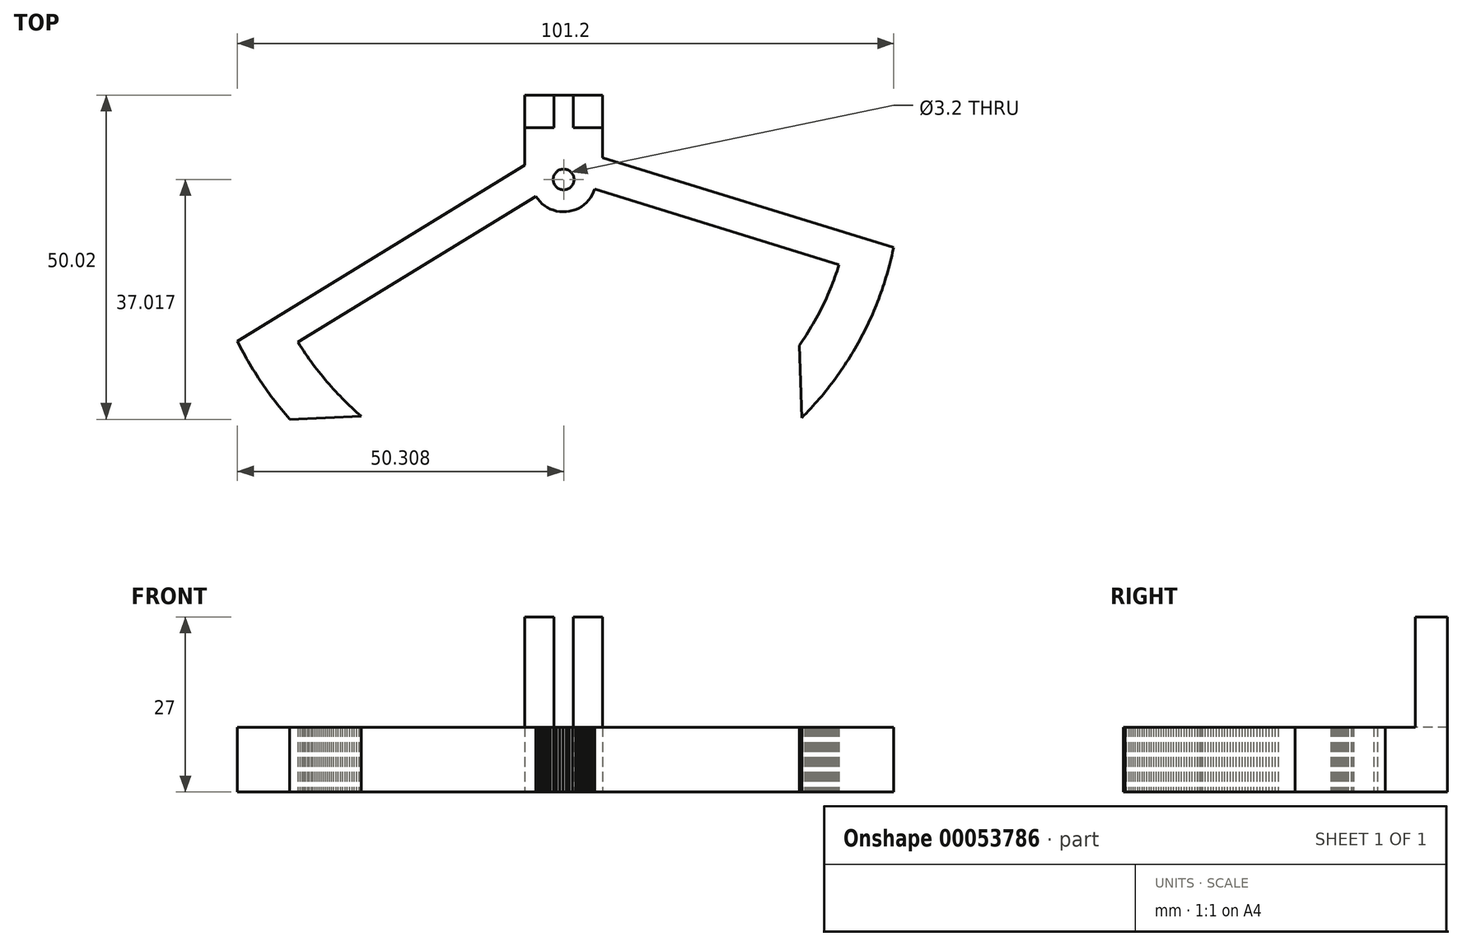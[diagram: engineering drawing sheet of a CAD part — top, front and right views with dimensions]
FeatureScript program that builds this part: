
annotation { "Feature Type Name" : "Feature", "Feature Type Description" : "" }
export const myFeature = defineFeature(function(context is Context, id is Id, definition is map)
    precondition{}
    {
        {
            var Q0;
            Q0=qCreatedBy(makeId("Top.planeOp"),FACE);
            var sketch = newSketch(context, id + "F0", { "sketchPlane" : qUnion([Q0])});
            skLineSegment(sketch, "E0", {"start": v(-31.49, -20.52) * mm, "end": v(-31.87, -20.2) * mm});
            skLineSegment(sketch, "E1", {"start": v(-31.87, -20.2) * mm, "end": v(-32.24, -19.86) * mm});
            skLineSegment(sketch, "E2", {"start": v(-32.24, -19.86) * mm, "end": v(-32.61, -19.53) * mm});
            skLineSegment(sketch, "E3", {"start": v(-32.61, -19.53) * mm, "end": v(-32.98, -19.2) * mm});
            skLineSegment(sketch, "E4", {"start": v(-32.98, -19.2) * mm, "end": v(-33.35, -18.85) * mm});
            skLineSegment(sketch, "E5", {"start": v(-33.35, -18.85) * mm, "end": v(-33.7, -18.5) * mm});
            skLineSegment(sketch, "E6", {"start": v(-33.7, -18.5) * mm, "end": v(-34.07, -18.15) * mm});
            skLineSegment(sketch, "E7", {"start": v(-34.07, -18.15) * mm, "end": v(-34.42, -17.8) * mm});
            skLineSegment(sketch, "E8", {"start": v(-34.42, -17.8) * mm, "end": v(-34.77, -17.44) * mm});
            skLineSegment(sketch, "E9", {"start": v(-34.77, -17.44) * mm, "end": v(-35.12, -17.08) * mm});
            skLineSegment(sketch, "E10", {"start": v(-35.12, -17.08) * mm, "end": v(-35.46, -16.72) * mm});
            skLineSegment(sketch, "E11", {"start": v(-35.46, -16.72) * mm, "end": v(-35.8, -16.35) * mm});
            skLineSegment(sketch, "E12", {"start": v(-35.8, -16.35) * mm, "end": v(-36.13, -15.98) * mm});
            skLineSegment(sketch, "E13", {"start": v(-36.13, -15.98) * mm, "end": v(-36.46, -15.6) * mm});
            skLineSegment(sketch, "E14", {"start": v(-36.46, -15.6) * mm, "end": v(-36.79, -15.23) * mm});
            skLineSegment(sketch, "E15", {"start": v(-36.79, -15.23) * mm, "end": v(-37.11, -14.84) * mm});
            skLineSegment(sketch, "E16", {"start": v(-37.11, -14.84) * mm, "end": v(-37.43, -14.46) * mm});
            skLineSegment(sketch, "E17", {"start": v(-37.43, -14.46) * mm, "end": v(-37.75, -14.07) * mm});
            skLineSegment(sketch, "E18", {"start": v(-37.75, -14.07) * mm, "end": v(-38.06, -13.68) * mm});
            skLineSegment(sketch, "E19", {"start": v(-38.06, -13.68) * mm, "end": v(-38.37, -13.28) * mm});
            skLineSegment(sketch, "E20", {"start": v(-38.37, -13.28) * mm, "end": v(-38.67, -12.89) * mm});
            skLineSegment(sketch, "E21", {"start": v(-38.67, -12.89) * mm, "end": v(-38.97, -12.49) * mm});
            skLineSegment(sketch, "E22", {"start": v(-38.97, -12.49) * mm, "end": v(-39.26, -12.08) * mm});
            skLineSegment(sketch, "E23", {"start": v(-39.26, -12.08) * mm, "end": v(-39.55, -11.67) * mm});
            skLineSegment(sketch, "E24", {"start": v(-39.55, -11.67) * mm, "end": v(-39.84, -11.26) * mm});
            skLineSegment(sketch, "E25", {"start": v(-39.84, -11.26) * mm, "end": v(-40.12, -10.85) * mm});
            skLineSegment(sketch, "E26", {"start": v(-40.12, -10.85) * mm, "end": v(-40.4, -10.44) * mm});
            skLineSegment(sketch, "E27", {"start": v(-40.4, -10.44) * mm, "end": v(-40.67, -10.02) * mm});
            skLineSegment(sketch, "E28", {"start": v(-40.67, -10.02) * mm, "end": v(-40.94, -9.6) * mm});
            skLineSegment(sketch, "E29", {"start": v(-40.94, -9.6) * mm, "end": v(-41.2, -9.17) * mm});
            skLineSegment(sketch, "E30", {"start": v(-41.2, -9.17) * mm, "end": v(-41.25, -9.1) * mm});
            skLineSegment(sketch, "E31", {"start": v(-41.25, -9.1) * mm, "end": v(-4.56, 13.4) * mm});
            skLineSegment(sketch, "E32", {"start": v(-4.56, 13.4) * mm, "end": v(-4.27, 12.98) * mm});
            skLineSegment(sketch, "E33", {"start": v(-4.27, 12.98) * mm, "end": v(-3.95, 12.6) * mm});
            skLineSegment(sketch, "E34", {"start": v(-3.95, 12.6) * mm, "end": v(-3.6, 12.25) * mm});
            skLineSegment(sketch, "E35", {"start": v(-3.6, 12.25) * mm, "end": v(-3.2, 11.94) * mm});
            skLineSegment(sketch, "E36", {"start": v(-3.2, 11.94) * mm, "end": v(-2.78, 11.67) * mm});
            skLineSegment(sketch, "E37", {"start": v(-2.78, 11.67) * mm, "end": v(-2.34, 11.44) * mm});
            skLineSegment(sketch, "E38", {"start": v(-2.34, 11.44) * mm, "end": v(-1.87, 11.26) * mm});
            skLineSegment(sketch, "E39", {"start": v(-1.87, 11.26) * mm, "end": v(-1.39, 11.13) * mm});
            skLineSegment(sketch, "E40", {"start": v(-1.39, 11.13) * mm, "end": v(-0.9, 11.04) * mm});
            skLineSegment(sketch, "E41", {"start": v(-0.9, 11.04) * mm, "end": v(-0.4, 11) * mm});
            skLineSegment(sketch, "E42", {"start": v(-0.4, 11) * mm, "end": v(0.1, 11.02) * mm});
            skLineSegment(sketch, "E43", {"start": v(0.1, 11.02) * mm, "end": v(0.6, 11.09) * mm});
            skLineSegment(sketch, "E44", {"start": v(0.6, 11.09) * mm, "end": v(1.08, 11.2) * mm});
            skLineSegment(sketch, "E45", {"start": v(1.08, 11.2) * mm, "end": v(1.56, 11.36) * mm});
            skLineSegment(sketch, "E46", {"start": v(1.56, 11.36) * mm, "end": v(2.01, 11.57) * mm});
            skLineSegment(sketch, "E47", {"start": v(2.01, 11.57) * mm, "end": v(2.44, 11.82) * mm});
            skLineSegment(sketch, "E48", {"start": v(2.44, 11.82) * mm, "end": v(2.85, 12.12) * mm});
            skLineSegment(sketch, "E49", {"start": v(2.85, 12.12) * mm, "end": v(3.22, 12.45) * mm});
            skLineSegment(sketch, "E50", {"start": v(3.22, 12.45) * mm, "end": v(3.56, 12.82) * mm});
            skLineSegment(sketch, "E51", {"start": v(3.56, 12.82) * mm, "end": v(3.86, 13.22) * mm});
            skLineSegment(sketch, "E52", {"start": v(3.86, 13.22) * mm, "end": v(4.12, 13.65) * mm});
            skLineSegment(sketch, "E53", {"start": v(4.12, 13.65) * mm, "end": v(4.33, 14.1) * mm});
            skLineSegment(sketch, "E54", {"start": v(4.33, 14.1) * mm, "end": v(4.48, 14.53) * mm});
            skLineSegment(sketch, "E55", {"start": v(4.48, 14.53) * mm, "end": v(42.19, 2.87) * mm});
            skLineSegment(sketch, "E56", {"start": v(42.19, 2.87) * mm, "end": v(42.04, 2.39) * mm});
            skLineSegment(sketch, "E57", {"start": v(42.04, 2.39) * mm, "end": v(41.88, 1.91) * mm});
            skLineSegment(sketch, "E58", {"start": v(41.88, 1.91) * mm, "end": v(41.72, 1.44) * mm});
            skLineSegment(sketch, "E59", {"start": v(41.72, 1.44) * mm, "end": v(41.55, 0.97) * mm});
            skLineSegment(sketch, "E60", {"start": v(41.55, 0.97) * mm, "end": v(41.38, 0.5) * mm});
            skLineSegment(sketch, "E61", {"start": v(41.38, 0.5) * mm, "end": v(41.2, 0.03) * mm});
            skLineSegment(sketch, "E62", {"start": v(41.2, 0.03) * mm, "end": v(41.02, -0.43) * mm});
            skLineSegment(sketch, "E63", {"start": v(41.02, -0.43) * mm, "end": v(40.83, -0.9) * mm});
            skLineSegment(sketch, "E64", {"start": v(40.83, -0.9) * mm, "end": v(40.64, -1.36) * mm});
            skLineSegment(sketch, "E65", {"start": v(40.64, -1.36) * mm, "end": v(40.44, -1.82) * mm});
            skLineSegment(sketch, "E66", {"start": v(40.44, -1.82) * mm, "end": v(40.24, -2.27) * mm});
            skLineSegment(sketch, "E67", {"start": v(40.24, -2.27) * mm, "end": v(40.03, -2.73) * mm});
            skLineSegment(sketch, "E68", {"start": v(40.03, -2.73) * mm, "end": v(39.82, -3.18) * mm});
            skLineSegment(sketch, "E69", {"start": v(39.82, -3.18) * mm, "end": v(39.6, -3.63) * mm});
            skLineSegment(sketch, "E70", {"start": v(39.6, -3.63) * mm, "end": v(39.38, -4.08) * mm});
            skLineSegment(sketch, "E71", {"start": v(39.38, -4.08) * mm, "end": v(39.15, -4.52) * mm});
            skLineSegment(sketch, "E72", {"start": v(39.15, -4.52) * mm, "end": v(38.92, -4.97) * mm});
            skLineSegment(sketch, "E73", {"start": v(38.92, -4.97) * mm, "end": v(38.68, -5.4) * mm});
            skLineSegment(sketch, "E74", {"start": v(38.68, -5.4) * mm, "end": v(38.43, -5.84) * mm});
            skLineSegment(sketch, "E75", {"start": v(38.43, -5.84) * mm, "end": v(38.19, -6.28) * mm});
            skLineSegment(sketch, "E76", {"start": v(38.19, -6.28) * mm, "end": v(37.93, -6.7) * mm});
            skLineSegment(sketch, "E77", {"start": v(37.93, -6.7) * mm, "end": v(37.68, -7.14) * mm});
            skLineSegment(sketch, "E78", {"start": v(37.68, -7.14) * mm, "end": v(37.41, -7.56) * mm});
            skLineSegment(sketch, "E79", {"start": v(37.41, -7.56) * mm, "end": v(37.15, -7.98) * mm});
            skLineSegment(sketch, "E80", {"start": v(37.15, -7.98) * mm, "end": v(36.87, -8.4) * mm});
            skLineSegment(sketch, "E81", {"start": v(36.87, -8.4) * mm, "end": v(36.6, -8.82) * mm});
            skLineSegment(sketch, "E82", {"start": v(36.6, -8.82) * mm, "end": v(36.32, -9.23) * mm});
            skLineSegment(sketch, "E83", {"start": v(36.32, -9.23) * mm, "end": v(36.05, -9.62) * mm});
            skLineSegment(sketch, "E84", {"start": v(36.05, -9.62) * mm, "end": v(36.42, -20.76) * mm});
            skLineSegment(sketch, "E85", {"start": v(36.42, -20.76) * mm, "end": v(36.78, -20.4) * mm});
            skLineSegment(sketch, "E86", {"start": v(36.78, -20.4) * mm, "end": v(37.12, -20.05) * mm});
            skLineSegment(sketch, "E87", {"start": v(37.12, -20.05) * mm, "end": v(37.47, -19.69) * mm});
            skLineSegment(sketch, "E88", {"start": v(37.47, -19.69) * mm, "end": v(37.81, -19.32) * mm});
            skLineSegment(sketch, "E89", {"start": v(37.81, -19.32) * mm, "end": v(38.15, -18.96) * mm});
            skLineSegment(sketch, "E90", {"start": v(38.15, -18.96) * mm, "end": v(38.48, -18.58) * mm});
            skLineSegment(sketch, "E91", {"start": v(38.48, -18.58) * mm, "end": v(38.82, -18.2) * mm});
            skLineSegment(sketch, "E92", {"start": v(38.82, -18.2) * mm, "end": v(39.14, -17.83) * mm});
            skLineSegment(sketch, "E93", {"start": v(39.14, -17.83) * mm, "end": v(39.47, -17.45) * mm});
            skLineSegment(sketch, "E94", {"start": v(39.47, -17.45) * mm, "end": v(39.79, -17.07) * mm});
            skLineSegment(sketch, "E95", {"start": v(39.79, -17.07) * mm, "end": v(40.1, -16.68) * mm});
            skLineSegment(sketch, "E96", {"start": v(40.1, -16.68) * mm, "end": v(40.42, -16.29) * mm});
            skLineSegment(sketch, "E97", {"start": v(40.42, -16.29) * mm, "end": v(40.72, -15.9) * mm});
            skLineSegment(sketch, "E98", {"start": v(40.72, -15.9) * mm, "end": v(41.03, -15.5) * mm});
            skLineSegment(sketch, "E99", {"start": v(41.03, -15.5) * mm, "end": v(41.33, -15.1) * mm});
            skLineSegment(sketch, "E100", {"start": v(41.33, -15.1) * mm, "end": v(41.63, -14.7) * mm});
            skLineSegment(sketch, "E101", {"start": v(41.63, -14.7) * mm, "end": v(41.92, -14.3) * mm});
            skLineSegment(sketch, "E102", {"start": v(41.92, -14.3) * mm, "end": v(42.21, -13.89) * mm});
            skLineSegment(sketch, "E103", {"start": v(42.21, -13.89) * mm, "end": v(42.5, -13.48) * mm});
            skLineSegment(sketch, "E104", {"start": v(42.5, -13.48) * mm, "end": v(42.78, -13.06) * mm});
            skLineSegment(sketch, "E105", {"start": v(42.78, -13.06) * mm, "end": v(43.06, -12.65) * mm});
            skLineSegment(sketch, "E106", {"start": v(43.06, -12.65) * mm, "end": v(43.33, -12.23) * mm});
            skLineSegment(sketch, "E107", {"start": v(43.33, -12.23) * mm, "end": v(43.6, -11.8) * mm});
            skLineSegment(sketch, "E108", {"start": v(43.6, -11.8) * mm, "end": v(43.87, -11.38) * mm});
            skLineSegment(sketch, "E109", {"start": v(43.87, -11.38) * mm, "end": v(44.13, -10.96) * mm});
            skLineSegment(sketch, "E110", {"start": v(44.13, -10.96) * mm, "end": v(44.38, -10.53) * mm});
            skLineSegment(sketch, "E111", {"start": v(44.38, -10.53) * mm, "end": v(44.64, -10.1) * mm});
            skLineSegment(sketch, "E112", {"start": v(44.64, -10.1) * mm, "end": v(44.89, -9.66) * mm});
            skLineSegment(sketch, "E113", {"start": v(44.89, -9.66) * mm, "end": v(45.13, -9.23) * mm});
            skLineSegment(sketch, "E114", {"start": v(45.13, -9.23) * mm, "end": v(45.37, -8.8) * mm});
            skLineSegment(sketch, "E115", {"start": v(45.37, -8.8) * mm, "end": v(45.6, -8.35) * mm});
            skLineSegment(sketch, "E116", {"start": v(45.6, -8.35) * mm, "end": v(45.84, -7.9) * mm});
            skLineSegment(sketch, "E117", {"start": v(45.84, -7.9) * mm, "end": v(46.07, -7.46) * mm});
            skLineSegment(sketch, "E118", {"start": v(46.07, -7.46) * mm, "end": v(46.3, -7.01) * mm});
            skLineSegment(sketch, "E119", {"start": v(46.3, -7.01) * mm, "end": v(46.51, -6.57) * mm});
            skLineSegment(sketch, "E120", {"start": v(46.51, -6.57) * mm, "end": v(46.73, -6.11) * mm});
            skLineSegment(sketch, "E121", {"start": v(46.73, -6.11) * mm, "end": v(46.94, -5.66) * mm});
            skLineSegment(sketch, "E122", {"start": v(46.94, -5.66) * mm, "end": v(47.14, -5.2) * mm});
            skLineSegment(sketch, "E123", {"start": v(47.14, -5.2) * mm, "end": v(47.35, -4.75) * mm});
            skLineSegment(sketch, "E124", {"start": v(47.35, -4.75) * mm, "end": v(47.54, -4.29) * mm});
            skLineSegment(sketch, "E125", {"start": v(47.54, -4.29) * mm, "end": v(47.74, -3.83) * mm});
            skLineSegment(sketch, "E126", {"start": v(47.74, -3.83) * mm, "end": v(47.93, -3.36) * mm});
            skLineSegment(sketch, "E127", {"start": v(47.93, -3.36) * mm, "end": v(48.1, -2.9) * mm});
            skLineSegment(sketch, "E128", {"start": v(48.1, -2.9) * mm, "end": v(48.29, -2.43) * mm});
            skLineSegment(sketch, "E129", {"start": v(48.29, -2.43) * mm, "end": v(48.46, -1.96) * mm});
            skLineSegment(sketch, "E130", {"start": v(48.46, -1.96) * mm, "end": v(48.64, -1.5) * mm});
            skLineSegment(sketch, "E131", {"start": v(48.64, -1.5) * mm, "end": v(48.8, -1.02) * mm});
            skLineSegment(sketch, "E132", {"start": v(48.8, -1.02) * mm, "end": v(48.96, -0.55) * mm});
            skLineSegment(sketch, "E133", {"start": v(48.96, -0.55) * mm, "end": v(49.12, -0.07) * mm});
            skLineSegment(sketch, "E134", {"start": v(49.12, -0.07) * mm, "end": v(49.27, 0.4) * mm});
            skLineSegment(sketch, "E135", {"start": v(49.27, 0.4) * mm, "end": v(49.42, 0.88) * mm});
            skLineSegment(sketch, "E136", {"start": v(49.42, 0.88) * mm, "end": v(49.56, 1.36) * mm});
            skLineSegment(sketch, "E137", {"start": v(49.56, 1.36) * mm, "end": v(49.7, 1.84) * mm});
            skLineSegment(sketch, "E138", {"start": v(49.7, 1.84) * mm, "end": v(49.84, 2.32) * mm});
            skLineSegment(sketch, "E139", {"start": v(49.84, 2.32) * mm, "end": v(49.97, 2.8) * mm});
            skLineSegment(sketch, "E140", {"start": v(49.97, 2.8) * mm, "end": v(50.1, 3.29) * mm});
            skLineSegment(sketch, "E141", {"start": v(50.1, 3.29) * mm, "end": v(50.21, 3.77) * mm});
            skLineSegment(sketch, "E142", {"start": v(50.21, 3.77) * mm, "end": v(50.33, 4.26) * mm});
            skLineSegment(sketch, "E143", {"start": v(50.33, 4.26) * mm, "end": v(50.44, 4.75) * mm});
            skLineSegment(sketch, "E144", {"start": v(50.44, 4.75) * mm, "end": v(50.54, 5.24) * mm});
            skLineSegment(sketch, "E145", {"start": v(50.54, 5.24) * mm, "end": v(50.6, 5.5) * mm});
            skLineSegment(sketch, "E146", {"start": v(50.6, 5.5) * mm, "end": v(1.19, 20.78) * mm});
            skLineSegment(sketch, "E147", {"start": v(1.19, 20.78) * mm, "end": v(0.7, 20.9) * mm});
            skLineSegment(sketch, "E148", {"start": v(0.7, 20.9) * mm, "end": v(0.2, 20.98) * mm});
            skLineSegment(sketch, "E149", {"start": v(0.2, 20.98) * mm, "end": v(-0.3, 21) * mm});
            skLineSegment(sketch, "E150", {"start": v(-0.3, 21) * mm, "end": v(-0.8, 20.98) * mm});
            skLineSegment(sketch, "E151", {"start": v(-0.8, 20.98) * mm, "end": v(-1.29, 20.9) * mm});
            skLineSegment(sketch, "E152", {"start": v(-1.29, 20.9) * mm, "end": v(-1.77, 20.78) * mm});
            skLineSegment(sketch, "E153", {"start": v(-1.77, 20.78) * mm, "end": v(-2.24, 20.61) * mm});
            skLineSegment(sketch, "E154", {"start": v(-2.24, 20.61) * mm, "end": v(-2.69, 20.4) * mm});
            skLineSegment(sketch, "E155", {"start": v(-2.69, 20.4) * mm, "end": v(-2.9, 20.27) * mm});
            skLineSegment(sketch, "E156", {"start": v(-2.9, 20.27) * mm, "end": v(-50.6, -8.96) * mm});
            skLineSegment(sketch, "E157", {"start": v(-50.6, -8.96) * mm, "end": v(-50.37, -9.4) * mm});
            skLineSegment(sketch, "E158", {"start": v(-50.37, -9.4) * mm, "end": v(-50.14, -9.85) * mm});
            skLineSegment(sketch, "E159", {"start": v(-50.14, -9.85) * mm, "end": v(-49.91, -10.3) * mm});
            skLineSegment(sketch, "E160", {"start": v(-49.91, -10.3) * mm, "end": v(-49.68, -10.73) * mm});
            skLineSegment(sketch, "E161", {"start": v(-49.68, -10.73) * mm, "end": v(-49.44, -11.17) * mm});
            skLineSegment(sketch, "E162", {"start": v(-49.44, -11.17) * mm, "end": v(-49.2, -11.6) * mm});
            skLineSegment(sketch, "E163", {"start": v(-49.2, -11.6) * mm, "end": v(-48.94, -12.04) * mm});
            skLineSegment(sketch, "E164", {"start": v(-48.94, -12.04) * mm, "end": v(-48.7, -12.47) * mm});
            skLineSegment(sketch, "E165", {"start": v(-48.7, -12.47) * mm, "end": v(-48.44, -12.9) * mm});
            skLineSegment(sketch, "E166", {"start": v(-48.44, -12.9) * mm, "end": v(-48.18, -13.33) * mm});
            skLineSegment(sketch, "E167", {"start": v(-48.18, -13.33) * mm, "end": v(-47.92, -13.76) * mm});
            skLineSegment(sketch, "E168", {"start": v(-47.92, -13.76) * mm, "end": v(-47.65, -14.18) * mm});
            skLineSegment(sketch, "E169", {"start": v(-47.65, -14.18) * mm, "end": v(-47.38, -14.6) * mm});
            skLineSegment(sketch, "E170", {"start": v(-47.38, -14.6) * mm, "end": v(-47.1, -15.02) * mm});
            skLineSegment(sketch, "E171", {"start": v(-47.1, -15.02) * mm, "end": v(-46.83, -15.43) * mm});
            skLineSegment(sketch, "E172", {"start": v(-46.83, -15.43) * mm, "end": v(-46.54, -15.85) * mm});
            skLineSegment(sketch, "E173", {"start": v(-46.54, -15.85) * mm, "end": v(-46.26, -16.26) * mm});
            skLineSegment(sketch, "E174", {"start": v(-46.26, -16.26) * mm, "end": v(-45.97, -16.66) * mm});
            skLineSegment(sketch, "E175", {"start": v(-45.97, -16.66) * mm, "end": v(-45.68, -17.07) * mm});
            skLineSegment(sketch, "E176", {"start": v(-45.68, -17.07) * mm, "end": v(-45.38, -17.47) * mm});
            skLineSegment(sketch, "E177", {"start": v(-45.38, -17.47) * mm, "end": v(-45.08, -17.87) * mm});
            skLineSegment(sketch, "E178", {"start": v(-45.08, -17.87) * mm, "end": v(-44.78, -18.27) * mm});
            skLineSegment(sketch, "E179", {"start": v(-44.78, -18.27) * mm, "end": v(-44.47, -18.66) * mm});
            skLineSegment(sketch, "E180", {"start": v(-44.47, -18.66) * mm, "end": v(-44.16, -19.06) * mm});
            skLineSegment(sketch, "E181", {"start": v(-44.16, -19.06) * mm, "end": v(-43.85, -19.45) * mm});
            skLineSegment(sketch, "E182", {"start": v(-43.85, -19.45) * mm, "end": v(-43.53, -19.83) * mm});
            skLineSegment(sketch, "E183", {"start": v(-43.53, -19.83) * mm, "end": v(-43.2, -20.22) * mm});
            skLineSegment(sketch, "E184", {"start": v(-43.2, -20.22) * mm, "end": v(-42.88, -20.6) * mm});
            skLineSegment(sketch, "E185", {"start": v(-42.88, -20.6) * mm, "end": v(-42.56, -20.97) * mm});
            skLineSegment(sketch, "E186", {"start": v(-42.56, -20.97) * mm, "end": v(-42.53, -21) * mm});
            skLineSegment(sketch, "E187", {"start": v(-42.53, -21) * mm, "end": v(-31.49, -20.52) * mm});
            skPoint(sketch, "E188", {"position": v(-0.3, 16) * mm});
            skLineSegment(sketch, "E189", {"start": v(1.2, 29) * mm, "end": v(1.2, 24) * mm});
            skPoint(sketch, "E190", {"position": v(-0.3, 15) * mm});
            skLineSegment(sketch, "E191", {"start": v(-1.8, 29) * mm, "end": v(-1.8, 24) * mm});
            skLineSegment(sketch, "E192", {"start": v(-6.3, 29) * mm, "end": v(5.7, 29) * mm});
            skLineSegment(sketch, "E193", {"start": v(-6.3, 15) * mm, "end": v(-6.3, 29) * mm});
            skLineSegment(sketch, "E194", {"start": v(5.7, 15) * mm, "end": v(5.7, 29) * mm});
            skLineSegment(sketch, "E195", {"start": v(-6.3, 16) * mm, "end": v(5.7, 16) * mm, "construction": true});
            skLineSegment(sketch, "E196", {"start": v(-6.3, 15) * mm, "end": v(5.7, 15) * mm});
            skLineSegment(sketch, "E197", {"start": v(-6.3, 24) * mm, "end": v(5.7, 24) * mm});
            skLineSegment(sketch, "E198", {"start": v(-0.3, 15) * mm, "end": v(-0.3, 29) * mm, "construction": true});
            skLineSegment(sketch, "E199", {"start": v(-4.85, 15) * mm, "end": v(4.26, 15) * mm, "construction": true});
            skCircle(sketch, "E200", {"center": v(-0.3, 16) * mm, "radius": 1.6 * mm});
            skSolve(sketch);
        }
        {
            var Q0;
            Q0=makeQuery(id+"F0.imprint","IMPRINT",FACE,{"disambiguationData":[TD([[makeQuery(id+"F0.imprint","IMPRINT",EDGE,{"derivedFrom":sQuery(id+"F0.wireOp",EDGE,"E0")}),1.0]])]});
            var Q1;
            {var subQ5=sQuery(id+"F0.wireOp",EDGE,"E147");Q1=makeQuery(id+"F0.imprint","IMPRINT",FACE,{"disambiguationData":[TD([[makeQuery(id+"F0.imprint","IMPRINT",EDGE,{"derivedFrom":subQ5}),1.0]])]});}
            var Q2;
            {var subQ1=sQuery(id+"F0.wireOp",EDGE,"E147");Q2=makeQuery(id+"F0.imprint","IMPRINT",FACE,{"disambiguationData":[TD([[makeQuery(id+"F0.imprint","IMPRINT",EDGE,{"derivedFrom":subQ1}),-1.0]])]});}
            var Q3;
            {var subQ0=sQuery(id+"F0.wireOp",EDGE,"E189");Q3=makeQuery(id+"F0.imprint","IMPRINT",FACE,{"disambiguationData":[TD([[makeQuery(id+"F0.imprint","IMPRINT",EDGE,{"derivedFrom":subQ0}),-1.0]])]});}
            extrude(context, id + "F1", {"entities" : qUnion([Q0, Q1, Q2, Q3]), "depth" : 10 * mm});
        }
        {
            var Q0;
            {var subQ0=sQuery(id+"F0.wireOp",EDGE,"E191");Q0=makeQuery(id+"F0.imprint","IMPRINT",FACE,{"disambiguationData":[TD([[makeQuery(id+"F0.imprint","IMPRINT",EDGE,{"derivedFrom":subQ0}),-1.0]])]});}
            var Q1;
            {var subQ0=sQuery(id+"F0.wireOp",EDGE,"E189");Q1=makeQuery(id+"F0.imprint","IMPRINT",FACE,{"disambiguationData":[TD([[makeQuery(id+"F0.imprint","IMPRINT",EDGE,{"derivedFrom":subQ0}),1.0]])]});}
            extrude(context, id + "F2", {"entities" : qUnion([Q0, Q1]), "operationType" : NewBodyOperationType.ADD, "depth" : 27 * mm});
        }
    });
